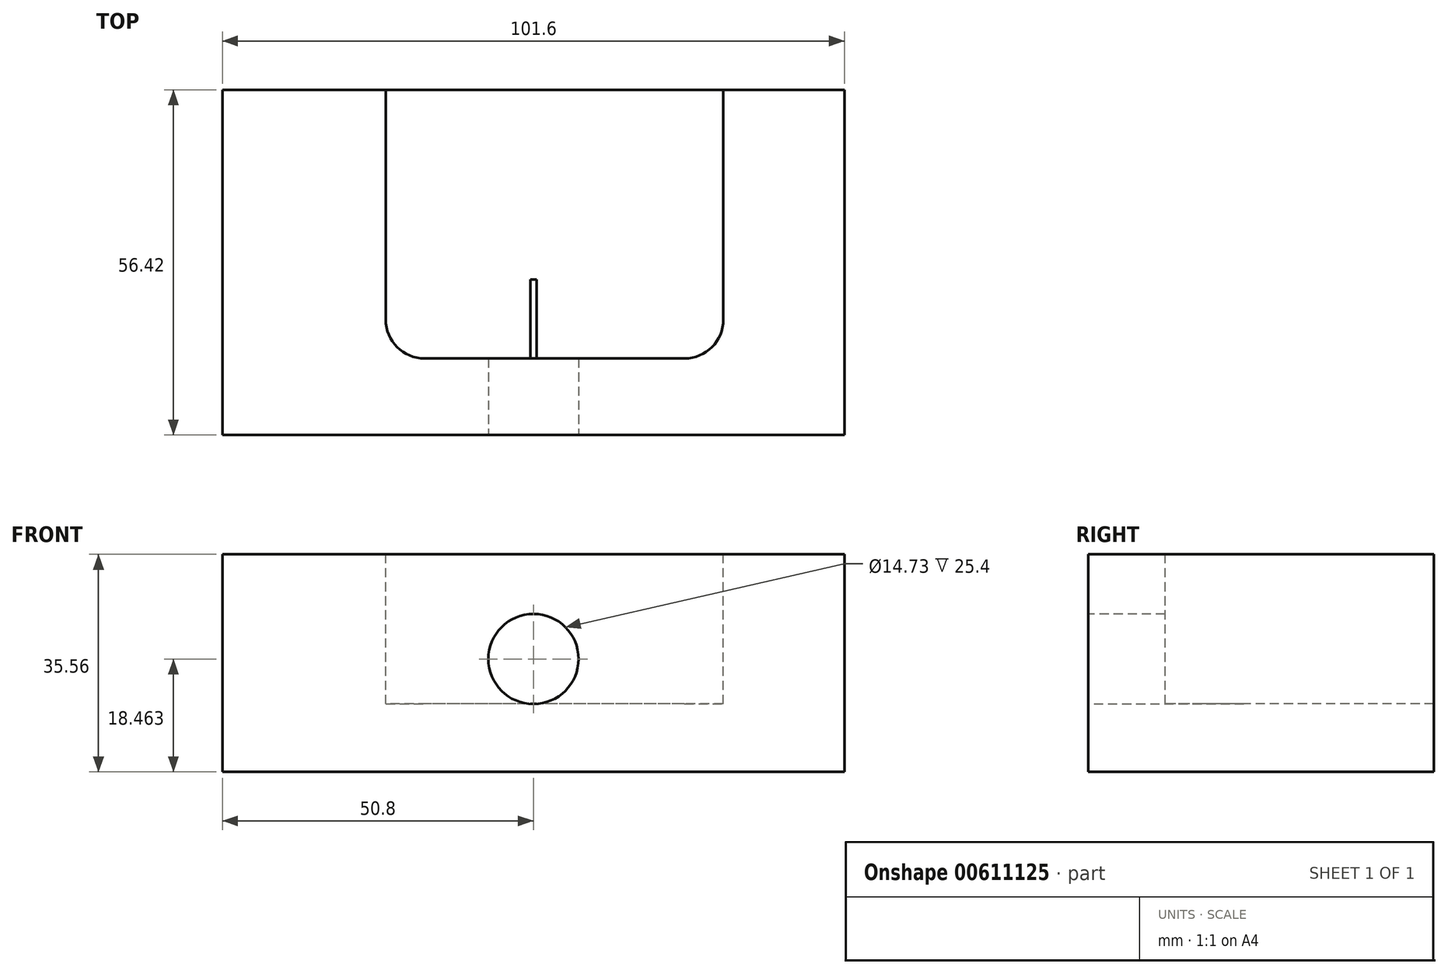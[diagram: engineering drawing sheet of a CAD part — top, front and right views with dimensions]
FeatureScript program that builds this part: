
annotation { "Feature Type Name" : "Feature", "Feature Type Description" : "" }
export const myFeature = defineFeature(function(context is Context, id is Id, definition is map)
    precondition{}
    {
        {
            var Q0;
            Q0=qCreatedBy(makeId("Right.planeOp"),FACE);
            var sketch = newSketch(context, id + "F0", { "sketchPlane" : qUnion([Q0])});
            skLineSegment(sketch, "E0.bottom", {"start": v(0, 0) * mm, "end": v(56.42, 0) * mm});
            skLineSegment(sketch, "E0.top", {"start": v(0, 35.56) * mm, "end": v(56.42, 35.56) * mm});
            skLineSegment(sketch, "E0.left", {"start": v(0, 0) * mm, "end": v(0, 35.56) * mm});
            skLineSegment(sketch, "E0.right", {"start": v(56.42, 0) * mm, "end": v(56.42, 35.56) * mm});
            skSolve(sketch);
        }
        {
            var Q0;
            Q0=makeQuery(id+"F0.imprint","IMPRINT",FACE,{"disambiguationData":[TD([[makeQuery(id+"F0.imprint","IMPRINT",EDGE,{"derivedFrom":sQuery(id+"F0.wireOp",EDGE,"E0.bottom")}),1.0]])]});
            extrude(context, id + "F1", {"entities" : qUnion([Q0]), "depth" : 101.6 * mm, "offsetDistance" : 25.4 * mm});
        }
        {
            var Q0;
            Q0=makeQuery(id+"F1.opExtrude","SWEPT_FACE",FACE,{"disambiguationData":[OSD([sQuery(id+"F0.wireOp",EDGE,"E0.top")])]});
            var sketch = newSketch(context, id + "F2", { "sketchPlane" : qUnion([Q0])});
            skLineSegment(sketch, "E1.bottom", {"start": v(81.83, 56.42) * mm, "end": v(26.68, 56.42) * mm});
            skLineSegment(sketch, "E1.top", {"start": v(75.48, 12.52) * mm, "end": v(33.03, 12.52) * mm});
            skLineSegment(sketch, "E1.left", {"start": v(81.83, 56.42) * mm, "end": v(81.83, 18.87) * mm});
            skLineSegment(sketch, "E1.right", {"start": v(26.68, 56.42) * mm, "end": v(26.68, 18.87) * mm});
            skPoint(sketch, "E2.visualSharp", {"position": v(81.83, 12.52) * mm});
            skArc(sketch, "E2.filletArc", {"start": v(75.48, 12.52) * mm, "mid": v(79.97, 14.38) * mm, "end": v(81.83, 18.87) * mm});
            skPoint(sketch, "E3.visualSharp", {"position": v(26.68, 12.52) * mm});
            skArc(sketch, "E3.filletArc", {"start": v(26.68, 18.87) * mm, "mid": v(28.54, 14.38) * mm, "end": v(33.03, 12.52) * mm});
            skSolve(sketch);
        }
        {
            var Q0;
            Q0=makeQuery(id+"F2.imprint","IMPRINT",FACE,{"disambiguationData":[TD([[makeQuery(id+"F2.imprint","IMPRINT",EDGE,{"derivedFrom":sQuery(id+"F2.wireOp",EDGE,"E1.bottom")}),1.0]])]});
            extrude(context, id + "F3", {"entities" : qUnion([Q0]), "operationType" : NewBodyOperationType.REMOVE, "oppositeDirection" : true, "depth" : 24.44 * mm, "offsetDistance" : 25.4 * mm});
        }
        {
            var Q0;
            Q0=makeQuery(id+"F1.opExtrude","SWEPT_FACE",FACE,{"disambiguationData":[OSD([sQuery(id+"F0.wireOp",EDGE,"E0.left")])]});
            var sketch = newSketch(context, id + "F4", { "sketchPlane" : qUnion([Q0])});
            skCircle(sketch, "E4", {"center": v(50.8, 18.46) * mm, "radius": 7.37 * mm});
            skPoint(sketch, "E4.centerSnap0", {"position": v(50.8, 0) * mm});
            skSolve(sketch);
        }
        {
            var Q0;
            Q0=makeQuery(id+"F4.imprint","IMPRINT",FACE,{"disambiguationData":[TD([[makeQuery(id+"F4.imprint","IMPRINT",EDGE,{"derivedFrom":sQuery(id+"F4.wireOp",EDGE,"E4")}),1.0]])]});
            extrude(context, id + "F5", {"entities" : qUnion([Q0]), "operationType" : NewBodyOperationType.REMOVE, "oppositeDirection" : true, "depth" : 25.4 * mm, "offsetDistance" : 25.4 * mm});
        }
    });
